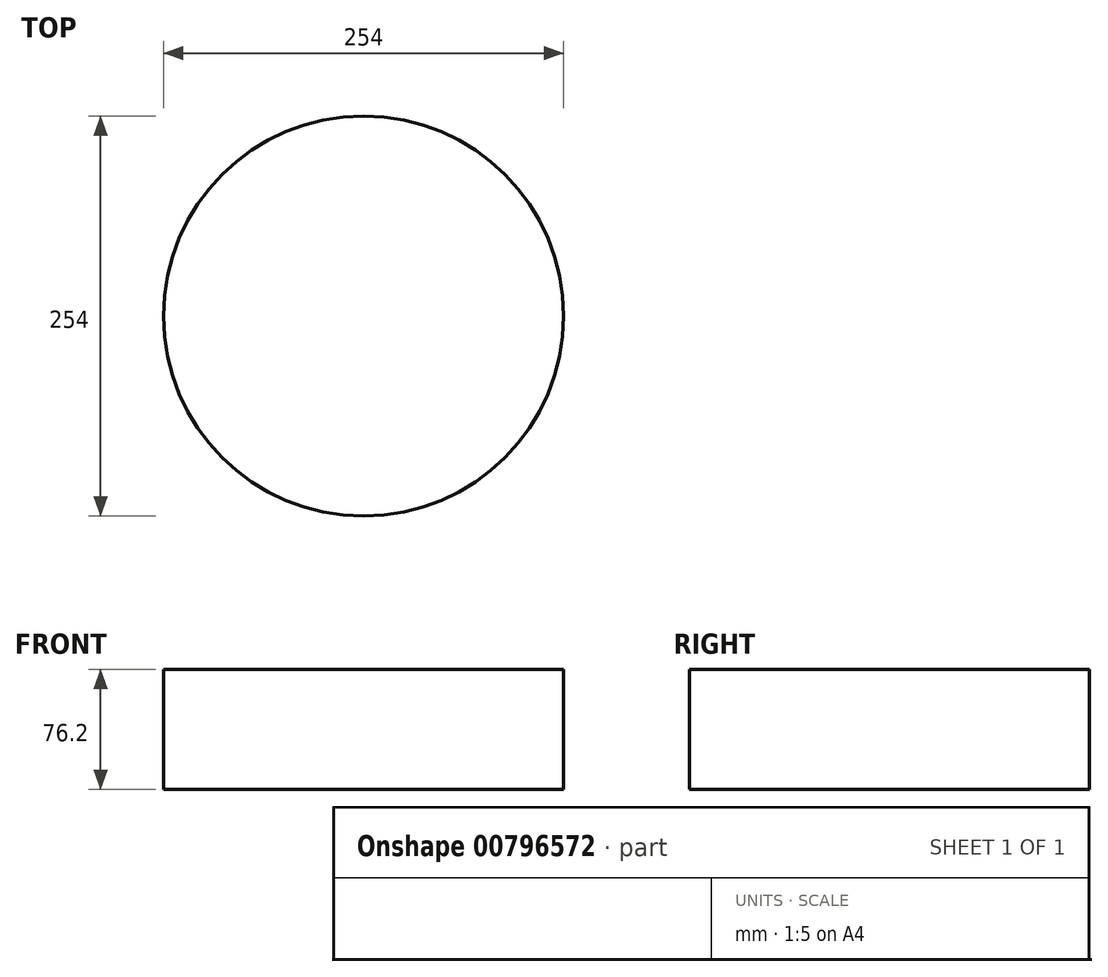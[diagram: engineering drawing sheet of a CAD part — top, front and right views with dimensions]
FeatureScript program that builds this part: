
annotation { "Feature Type Name" : "Feature", "Feature Type Description" : "" }
export const myFeature = defineFeature(function(context is Context, id is Id, definition is map)
    precondition{}
    {
        {
            var Q0;
            Q0=qCreatedBy(makeId("Top.planeOp"),FACE);
            var sketch = newSketch(context, id + "F0", { "sketchPlane" : qUnion([Q0])});
            skCircle(sketch, "E0", {"center": v(0, 0) * mm, "radius": 127 * mm});
            skPoint(sketch, "E0.first.point", {"position": v(-64.63, 109.33) * mm});
            skPoint(sketch, "E0.second.point", {"position": v(105.07, -71.34) * mm});
            skPoint(sketch, "E0.third.point", {"position": v(-72.09, -104.56) * mm});
            skSolve(sketch);
        }
        {
            var Q0;
            Q0=makeQuery(id+"F0.imprint","IMPRINT",FACE,{"disambiguationData":[TD([[makeQuery(id+"F0.imprint","IMPRINT",EDGE,{"derivedFrom":sQuery(id+"F0.wireOp",EDGE,"E0")}),1.0]])]});
            extrude(context, id + "F1", {"entities" : qUnion([Q0]), "endBound" : BoundingType.SYMMETRIC, "oppositeDirection" : true, "depth" : 76.2 * mm, "offsetDistance" : 25.4 * mm});
        }
    });
